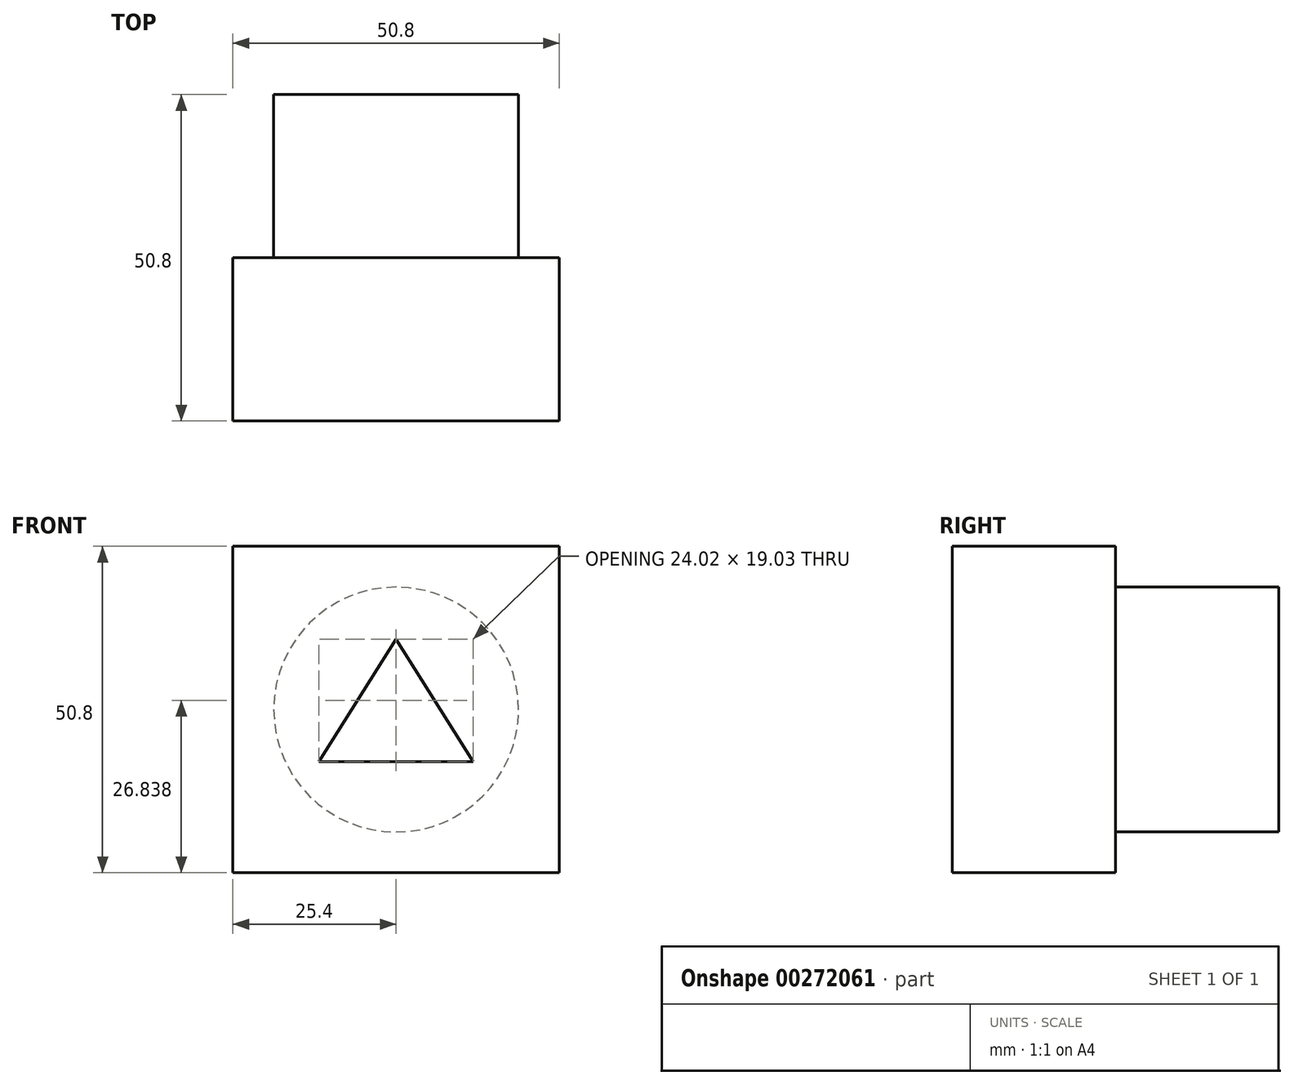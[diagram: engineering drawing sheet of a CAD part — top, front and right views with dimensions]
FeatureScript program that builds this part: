
annotation { "Feature Type Name" : "Feature", "Feature Type Description" : "" }
export const myFeature = defineFeature(function(context is Context, id is Id, definition is map)
    precondition{}
    {
        {
            var Q0;
            Q0=qCreatedBy(makeId("Front.planeOp"),FACE);
            var sketch = newSketch(context, id + "F0", { "sketchPlane" : qUnion([Q0])});
            skLineSegment(sketch, "E0.bottom", {"start": v(-37.4, 27.03) * mm, "end": v(13.4, 27.03) * mm});
            skLineSegment(sketch, "E0.top", {"start": v(-37.4, -23.77) * mm, "end": v(13.4, -23.77) * mm});
            skLineSegment(sketch, "E0.left", {"start": v(-37.4, 27.03) * mm, "end": v(-37.4, -23.77) * mm});
            skLineSegment(sketch, "E0.right", {"start": v(13.4, 27.03) * mm, "end": v(13.4, -23.77) * mm});
            skCircle(sketch, "E1", {"center": v(-12, 1.63) * mm, "radius": 19.05 * mm});
            skLineSegment(sketch, "E2", {"start": v(-24.02, -6.45) * mm, "end": v(-12, 12.58) * mm});
            skLineSegment(sketch, "E3", {"start": v(-12, 12.58) * mm, "end": v(0, -6.45) * mm});
            skLineSegment(sketch, "E4", {"start": v(-24.02, -6.45) * mm, "end": v(0, -6.45) * mm});
            skSolve(sketch);
        }
        {
            var Q0;
            Q0=makeQuery(id+"F0.imprint","IMPRINT",FACE,{"disambiguationData":[TD([[makeQuery(id+"F0.imprint","IMPRINT",EDGE,{"derivedFrom":sQuery(id+"F0.wireOp",EDGE,"E0.bottom")}),-1.0]])]});
            var Q1;
            Q1=makeQuery(id+"F0.imprint","IMPRINT",FACE,{"disambiguationData":[TD([[makeQuery(id+"F0.imprint","IMPRINT",EDGE,{"derivedFrom":sQuery(id+"F0.wireOp",EDGE,"E1")}),1.0]])]});
            extrude(context, id + "F1", {"entities" : qUnion([Q0, Q1]), "depth" : 25.4 * mm});
        }
        {
            var Q0;
            Q0=makeQuery(id+"F0.imprint","IMPRINT",FACE,{"disambiguationData":[TD([[makeQuery(id+"F0.imprint","IMPRINT",EDGE,{"derivedFrom":sQuery(id+"F0.wireOp",EDGE,"E1")}),1.0]])]});
            extrude(context, id + "F2", {"entities" : qUnion([Q0]), "operationType" : NewBodyOperationType.ADD, "oppositeDirection" : true, "depth" : 25.4 * mm});
        }
    });
